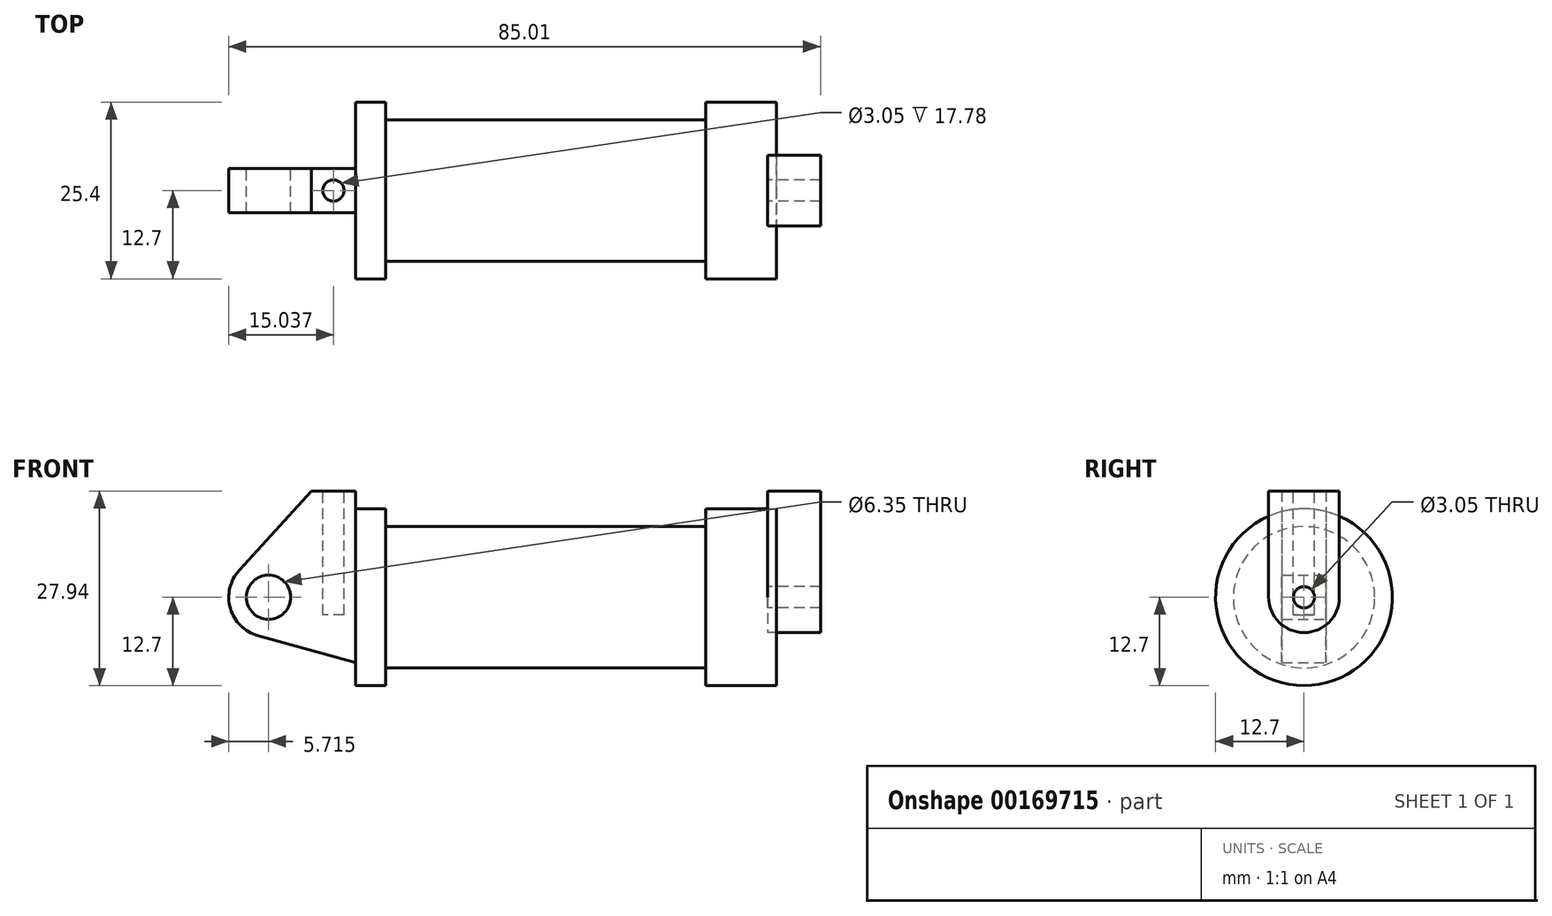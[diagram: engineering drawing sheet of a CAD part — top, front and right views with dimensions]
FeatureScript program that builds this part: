
annotation { "Feature Type Name" : "Feature", "Feature Type Description" : "" }
export const myFeature = defineFeature(function(context is Context, id is Id, definition is map)
    precondition{}
    {
        {
            var Q0;
            Q0=qCreatedBy(makeId("Front.planeOp"),FACE);
            var sketch = newSketch(context, id + "F0", { "sketchPlane" : qUnion([Q0])});
            skLineSegment(sketch, "E0", {"start": v(0, 0) * mm, "end": v(0, 12.7) * mm});
            skLineSegment(sketch, "E1", {"start": v(0, 12.7) * mm, "end": v(10.16, 12.7) * mm});
            skLineSegment(sketch, "E2", {"start": v(10.16, 12.7) * mm, "end": v(10.16, 10.16) * mm});
            skLineSegment(sketch, "E3", {"start": v(10.16, 10.16) * mm, "end": v(56.13, 10.16) * mm});
            skLineSegment(sketch, "E4", {"start": v(56.13, 10.16) * mm, "end": v(56.13, 12.7) * mm});
            skLineSegment(sketch, "E5", {"start": v(56.13, 12.7) * mm, "end": v(66.3, 12.7) * mm});
            skLineSegment(sketch, "E6", {"start": v(66.3, 12.7) * mm, "end": v(66.3, 0) * mm});
            skLineSegment(sketch, "E7", {"start": v(66.3, 0) * mm, "end": v(0, 0) * mm});
            skLineSegment(sketch, "E8", {"start": v(5.84, 15.24) * mm, "end": v(-0.5, 15.24) * mm});
            skLineSegment(sketch, "E9", {"start": v(-0.5, 15.24) * mm, "end": v(-10.88, 3.85) * mm});
            skLineSegment(sketch, "E10", {"start": v(0, 0) * mm, "end": v(-6.65, 0) * mm});
            skCircle(sketch, "E11", {"center": v(-6.65, 0) * mm, "radius": 5.72 * mm});
            skCircle(sketch, "E12", {"center": v(-6.65, 0) * mm, "radius": 3.18 * mm});
            skLineSegment(sketch, "E13", {"start": v(5.84, 15.24) * mm, "end": v(5.84, -9.4) * mm});
            skLineSegment(sketch, "E14", {"start": v(5.84, -9.4) * mm, "end": v(-8.18, -5.5) * mm});
            skSolve(sketch);
        }
        {
            var Q0;
            {var subQ0=sQuery(id+"F0.wireOp",EDGE,"E2");Q0=makeQuery(id+"F0.imprint","IMPRINT",FACE,{"disambiguationData":[TD([[makeQuery(id+"F0.imprint","IMPRINT",EDGE,{"derivedFrom":subQ0}),-1.0]])]});}
            var Q1;
            Q1=sQuery(id+"F0.wireOp",EDGE,"E7");
            revolve(context, id + "F1", {"entities" : qUnion([Q0]), "axis" : qUnion([Q1]), "revolveType" : RevolveType.FULL});
        }
        {
            var Q0;
            {var subQ0=sQuery(id+"F0.wireOp",EDGE,"E14");Q0=makeQuery(id+"F0.imprint","IMPRINT",FACE,{"disambiguationData":[TD([[makeQuery(id+"F0.imprint","IMPRINT",EDGE,{"derivedFrom":subQ0}),-1.0]])]});}
            var Q1;
            {var subQ0=sQuery(id+"F0.wireOp",EDGE,"E0");Q1=makeQuery(id+"F0.imprint","IMPRINT",FACE,{"disambiguationData":[TD([[makeQuery(id+"F0.imprint","IMPRINT",EDGE,{"derivedFrom":subQ0}),-1.0]])]});}
            var Q2;
            {var subQ3=sQuery(id+"F0.wireOp",EDGE,"E0");Q2=makeQuery(id+"F0.imprint","IMPRINT",FACE,{"disambiguationData":[TD([[makeQuery(id+"F0.imprint","IMPRINT",EDGE,{"derivedFrom":subQ3}),1.0]])]});}
            var Q3;
            {var subQ4=sQuery(id+"F0.wireOp",EDGE,"E12");Q3=makeQuery(id+"F0.imprint","IMPRINT",FACE,{"disambiguationData":[TD([[makeQuery(id+"F0.imprint","IMPRINT",EDGE,{"derivedFrom":subQ4}),-1.0]])]});}
            extrude(context, id + "F2", {"entities" : qUnion([Q0, Q1, Q2, Q3]), "operationType" : NewBodyOperationType.ADD, "endBound" : BoundingType.SYMMETRIC, "depth" : 6.35 * mm});
        }
        {
            var Q0;
            Q0=makeQuery(id+"F1.opRevolve","SWEPT_FACE",FACE,{"disambiguationData":[OSD([sQuery(id+"F0.wireOp",EDGE,"E6")])]});
            var sketch = newSketch(context, id + "F3", { "sketchPlane" : qUnion([Q0])});
            skCircle(sketch, "E15", {"center": v(0, 0) * mm, "radius": 5.08 * mm});
            skCircle(sketch, "E16", {"center": v(0, 0) * mm, "radius": 1.52 * mm});
            skLineSegment(sketch, "E17", {"start": v(0, 0) * mm, "end": v(-5.08, 0) * mm});
            skLineSegment(sketch, "E18", {"start": v(-5.08, 0) * mm, "end": v(-5.08, 15.24) * mm});
            skLineSegment(sketch, "E19.MirrorCS", {"start": v(5.08, 0) * mm, "end": v(5.08, 15.24) * mm});
            skLineSegment(sketch, "E20", {"start": v(-5.08, 15.24) * mm, "end": v(5.08, 15.24) * mm});
            skSolve(sketch);
        }
        {
            var Q0;
            Q0=makeQuery(id+"F2.opExtrude","SWEPT_FACE",FACE,{"disambiguationData":[OSD([sQuery(id+"F0.wireOp",EDGE,"E8")])]});
            var sketch = newSketch(context, id + "F4", { "sketchPlane" : qUnion([Q0])});
            skCircle(sketch, "E21", {"center": v(2.67, 0) * mm, "radius": 1.52 * mm});
            skPoint(sketch, "E21.centerSnap0", {"position": v(-0.5, 0) * mm});
            skPoint(sketch, "E21.centerSnap1", {"position": v(2.67, -3.18) * mm});
            skSolve(sketch);
        }
        {
            var Q0;
            Q0=makeQuery(id+"F4.imprint","IMPRINT",FACE,{"disambiguationData":[TD([[makeQuery(id+"F4.imprint","IMPRINT",EDGE,{"derivedFrom":sQuery(id+"F4.wireOp",EDGE,"E21")}),1.0]])]});
            var Q1;
            Q1=sQuery(id+"F4.wireOp",EDGE,"E21");
            extrude(context, id + "F5", {"entities" : qUnion([Q0]), "operationType" : NewBodyOperationType.REMOVE, "surfaceEntities" : qUnion([Q1]), "oppositeDirection" : true, "depth" : 17.78 * mm});
        }
        {
            var Q0;
            {var subQ0=sQuery(id+"F3.wireOp",EDGE,"E18");var subQ1=sQuery(id+"F3.wireOp",EDGE,"E15");var subQ2=makeQuery(id+"F3.imprint","INTERSECT",VERTEX,{"derivedFrom":[subQ1,subQ0]});Q0=makeQuery(id+"F3.imprint","IMPRINT",FACE,{"disambiguationData":[TD([[makeQuery(id+"F3.imprint","IMPRINT",EDGE,{"disambiguationData":[TD([[subQ2,1.0]])],"derivedFrom":subQ1}),-1.0]])]});}
            var Q1;
            {var subQ0=sQuery(id+"F3.wireOp",EDGE,"E20");Q1=makeQuery(id+"F3.imprint","IMPRINT",FACE,{"disambiguationData":[TD([[makeQuery(id+"F3.imprint","IMPRINT",EDGE,{"derivedFrom":subQ0}),-1.0]])]});}
            var Q2;
            Q2=makeQuery(id+"F3.imprint","IMPRINT",FACE,{"disambiguationData":[TD([[makeQuery(id+"F3.imprint","IMPRINT",EDGE,{"derivedFrom":sQuery(id+"F3.wireOp",EDGE,"E16")}),-1.0]])]});
            var Q3;
            Q3=sQuery(id+"F3.wireOp",EDGE,"E18");
            var Q4;
            Q4=sQuery(id+"F3.wireOp",EDGE,"E20");
            var Q5;
            Q5=sQuery(id+"F3.wireOp",EDGE,"E19.MirrorCS");
            var Q6;
            Q6=sQuery(id+"F3.wireOp",EDGE,"E15");
            var Q7;
            Q7=sQuery(id+"F3.wireOp",EDGE,"E16");
            extrude(context, id + "F6", {"entities" : qUnion([Q0, Q1, Q2]), "surfaceEntities" : qUnion([Q3, Q4, Q5, Q6, Q7]), "depth" : 6.35 * mm, "hasSecondDirection" : true, "secondDirectionOppositeDirection" : true, "secondDirectionDepth" : 1.27 * mm});
        }
    });
